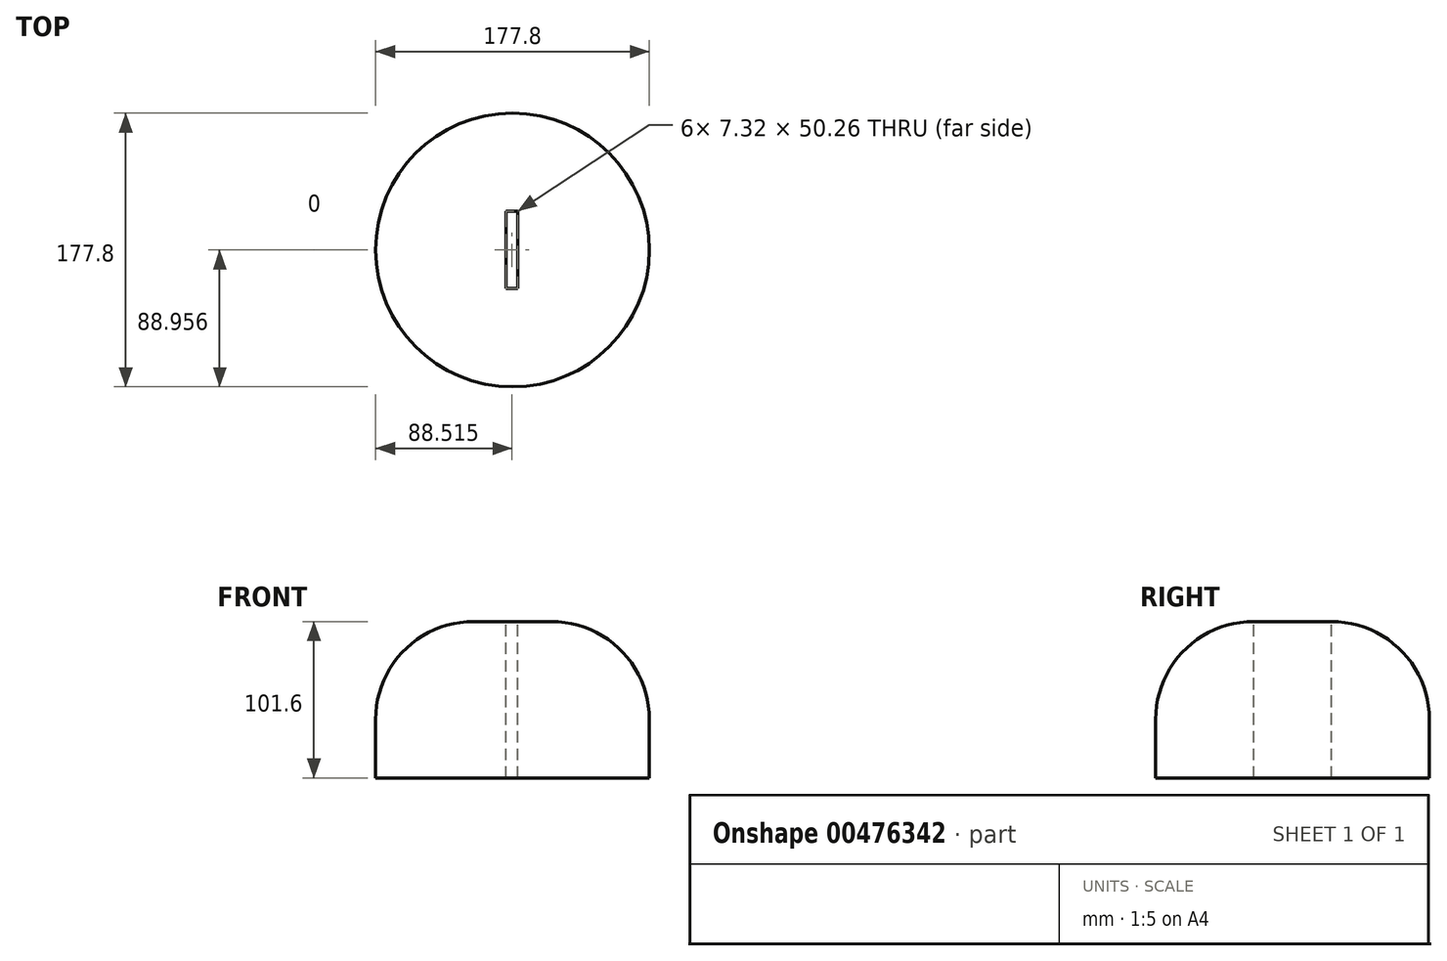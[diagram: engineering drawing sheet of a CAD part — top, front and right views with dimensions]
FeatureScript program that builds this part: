
annotation { "Feature Type Name" : "Feature", "Feature Type Description" : "" }
export const myFeature = defineFeature(function(context is Context, id is Id, definition is map)
    precondition{}
    {
        {
            var Q0;
            Q0=qCreatedBy(makeId("Top.planeOp"),FACE);
            var sketch = newSketch(context, id + "F0", { "sketchPlane" : qUnion([Q0])});
            skCircle(sketch, "E0", {"center": v(0, 0) * mm, "radius": 88.9 * mm});
            skSolve(sketch);
        }
        {
            var Q0;
            Q0 = qSketchRegion(id + "F0", true);
            extrude(context, id + "F1", {"entities" : qUnion([Q0]), "depth" : 101.6 * mm});
        }
        {
            var Q0;
            Q0=makeQuery(id+"F1.opExtrude","CAP_EDGE",EDGE,{"disambiguationData":[OSD([sQuery(id+"F0.wireOp",EDGE,"E0")])],"isStart":false});
            fillet(context, id + "F2", {"entities" : qUnion([Q0]), "radius" : 63.5 * mm, "tangentPropagation" : true, "allowEdgeOverflow" : false});
        }
        {
            var Q0;
            Q0=makeQuery(id+"F1.opExtrude","CAP_FACE",FACE,{"disambiguationData":[OSD([sQuery(id+"F0.wireOp",EDGE,"E0")])],"isStart":false});
            var sketch = newSketch(context, id + "F3", { "sketchPlane" : qUnion([Q0])});
            skLineSegment(sketch, "E1.bottom", {"start": v(3.28, 25.19) * mm, "end": v(-4.05, 25.19) * mm});
            skLineSegment(sketch, "E1.top", {"start": v(3.28, -25.08) * mm, "end": v(-4.05, -25.08) * mm});
            skLineSegment(sketch, "E1.left", {"start": v(3.28, 25.19) * mm, "end": v(3.28, -25.08) * mm});
            skLineSegment(sketch, "E1.right", {"start": v(-4.05, 25.19) * mm, "end": v(-4.05, -25.08) * mm});
            skSolve(sketch);
        }
        {
            var Q0;
            Q0 = qSketchRegion(id + "F3", true);
            extrude(context, id + "F4", {"entities" : qUnion([Q0]), "operationType" : NewBodyOperationType.REMOVE, "oppositeDirection" : true, "depth" : 101.6 * mm});
        }
    });
